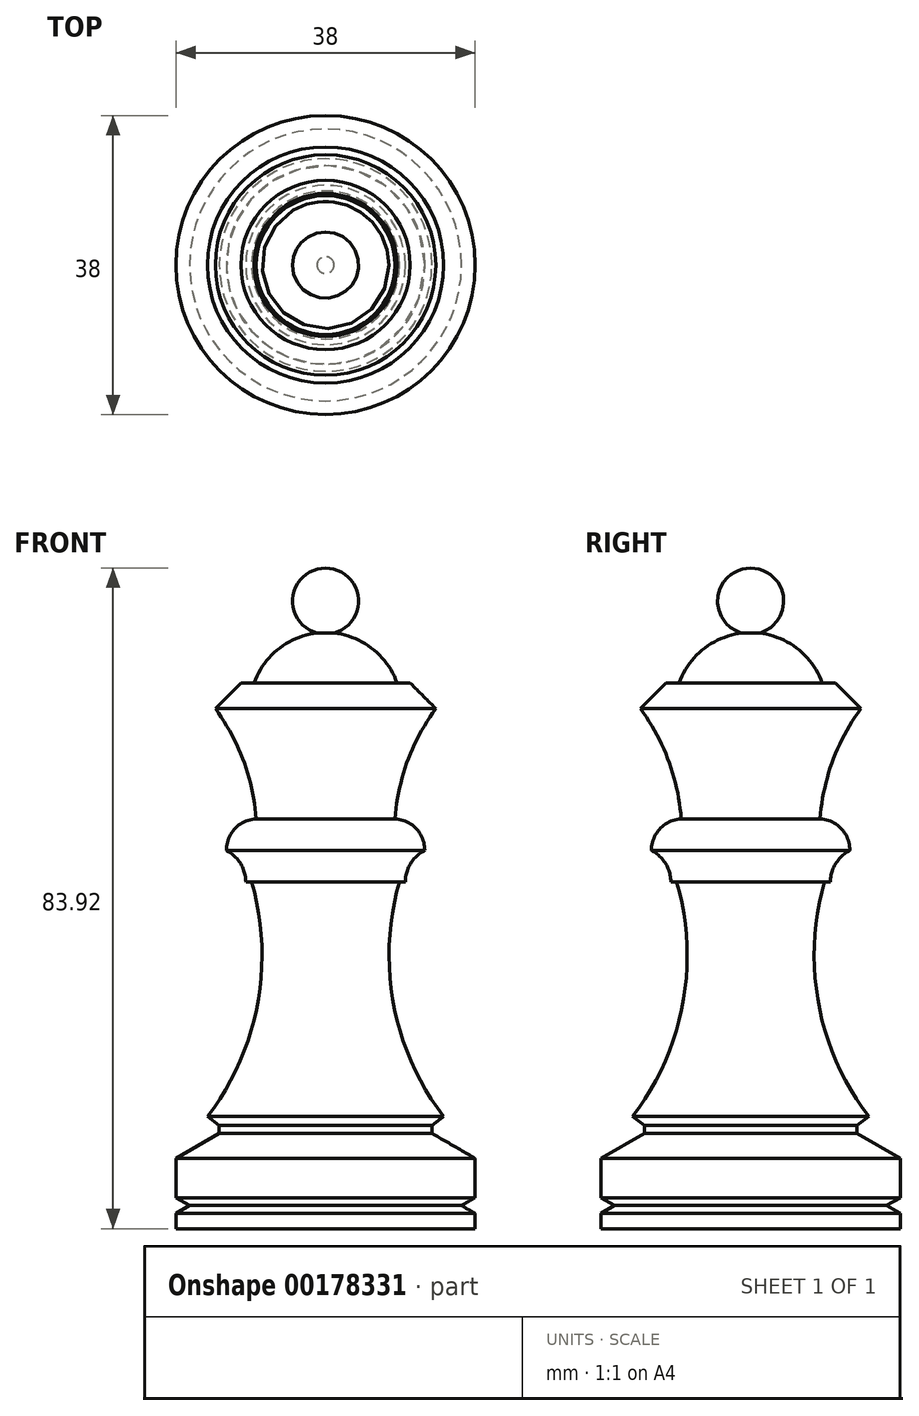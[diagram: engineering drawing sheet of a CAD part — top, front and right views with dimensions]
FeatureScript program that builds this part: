
annotation { "Feature Type Name" : "Feature", "Feature Type Description" : "" }
export const myFeature = defineFeature(function(context is Context, id is Id, definition is map)
    precondition{}
    {
        {
            var Q0;
            Q0=qCreatedBy(makeId("Front.planeOp"),FACE);
            var sketch = newSketch(context, id + "F0", { "sketchPlane" : qUnion([Q0])});
            skLineSegment(sketch, "E0", {"start": v(19, 1.94) * mm, "end": v(17.27, 2.94) * mm});
            skLineSegment(sketch, "E1", {"start": v(19, 3.94) * mm, "end": v(17.27, 2.94) * mm});
            skLineSegment(sketch, "E2", {"start": v(19, 3.94) * mm, "end": v(19, 8.94) * mm});
            skLineSegment(sketch, "E3", {"start": v(19, 8.94) * mm, "end": v(13.5, 12.11) * mm});
            skLineSegment(sketch, "E4", {"start": v(9.4, 44.07) * mm, "end": v(10.13, 44.07) * mm});
            skLineSegment(sketch, "E5", {"start": v(14.23, 48.24) * mm, "end": v(14.23, 48.04) * mm});
            skLineSegment(sketch, "E6", {"start": v(8.75, 52.07) * mm, "end": v(8.82, 52.07) * mm});
            skArc(sketch, "E7", {"start": v(14, 66.07) * mm, "mid": v(10.43, 59.44) * mm, "end": v(8.82, 52.07) * mm});
            skLineSegment(sketch, "E8", {"start": v(14, 66.07) * mm, "end": v(10.75, 69.32) * mm});
            skLineSegment(sketch, "E9", {"start": v(9.09, 69.32) * mm, "end": v(10.75, 69.32) * mm});
            skArc(sketch, "E10", {"start": v(1.08, 75.66) * mm, "mid": v(5.99, 73.64) * mm, "end": v(9.09, 69.32) * mm});
            skArc(sketch, "E11", {"start": v(1.08, 75.66) * mm, "mid": v(4.16, 80.26) * mm, "end": v(0, 83.92) * mm});
            skArc(sketch, "E12", {"start": v(9.4, 44.07) * mm, "mid": v(8.64, 28.5) * mm, "end": v(15, 14.25) * mm});
            skArc(sketch, "E13", {"start": v(8.82, 52.07) * mm, "mid": v(11.52, 50.81) * mm, "end": v(12.6, 48.04) * mm});
            skLineSegment(sketch, "E14", {"start": v(19, 0) * mm, "end": v(0, 0) * mm});
            skLineSegment(sketch, "E15", {"start": v(19, 0) * mm, "end": v(19, 1.94) * mm});
            skLineSegment(sketch, "E16", {"start": v(0, 83.92) * mm, "end": v(0, 0) * mm});
            skLineSegment(sketch, "E17", {"start": v(8.75, 52.07) * mm, "end": v(0, 52.07) * mm});
            skLineSegment(sketch, "E18", {"start": v(9.4, 44.07) * mm, "end": v(0, 44.07) * mm});
            skLineSegment(sketch, "E19", {"start": v(12.6, 48.04) * mm, "end": v(0, 48.04) * mm});
            skLineSegment(sketch, "E20", {"start": v(13.5, 12.11) * mm, "end": v(0, 12.11) * mm});
            skArc(sketch, "E21", {"start": v(12.6, 48.04) * mm, "mid": v(10.82, 46.4) * mm, "end": v(10.13, 44.07) * mm});
            skLineSegment(sketch, "E22", {"start": v(13.5, 12.11) * mm, "end": v(13.5, 13.11) * mm});
            skLineSegment(sketch, "E23", {"start": v(13.5, 13.11) * mm, "end": v(15, 14.25) * mm});
            skSolve(sketch);
        }
        {
            var Q0;
            Q0=makeQuery(id+"F0.imprint","IMPRINT",FACE,{"disambiguationData":[TD([[makeQuery(id+"F0.imprint","IMPRINT",EDGE,{"derivedFrom":sQuery(id+"F0.wireOp",EDGE,"E6")}),1.0]])]});
            var Q1;
            Q1=makeQuery(id+"F0.imprint","IMPRINT",FACE,{"disambiguationData":[TD([[makeQuery(id+"F0.imprint","IMPRINT",EDGE,{"derivedFrom":sQuery(id+"F0.wireOp",EDGE,"E6")}),-1.0]])]});
            var Q2;
            Q2=makeQuery(id+"F0.imprint","IMPRINT",FACE,{"disambiguationData":[TD([[makeQuery(id+"F0.imprint","IMPRINT",EDGE,{"derivedFrom":sQuery(id+"F0.wireOp",EDGE,"E4")}),1.0]])]});
            var Q3;
            Q3=makeQuery(id+"F0.imprint","IMPRINT",FACE,{"disambiguationData":[TD([[makeQuery(id+"F0.imprint","IMPRINT",EDGE,{"derivedFrom":sQuery(id+"F0.wireOp",EDGE,"E0")}),1.0]])]});
            var Q4;
            Q4=makeQuery(id+"F0.imprint","IMPRINT",FACE,{"disambiguationData":[TD([[makeQuery(id+"F0.imprint","IMPRINT",EDGE,{"derivedFrom":sQuery(id+"F0.wireOp",EDGE,"nyWY0tnP-Jj6n-QFmL-lNrs-mm1IDGyNNZQy")}),-1.0]])]});
            var Q5;
            Q5=makeQuery(id+"F0.imprint","IMPRINT",FACE,{"disambiguationData":[TD([[makeQuery(id+"F0.imprint","IMPRINT",EDGE,{"derivedFrom":sQuery(id+"F0.wireOp",EDGE,"E12")}),-1.0]])]});
            var Q6;
            Q6=sQuery(id+"F0.wireOp",EDGE,"E16");
            revolve(context, id + "F1", {"surfaceOperationType" : NewSurfaceOperationType.NEW, "entities" : qUnion([Q0, Q1, Q2, Q3, Q4, Q5]), "axis" : qUnion([Q6]), "revolveType" : RevolveType.FULL});
        }
    });
